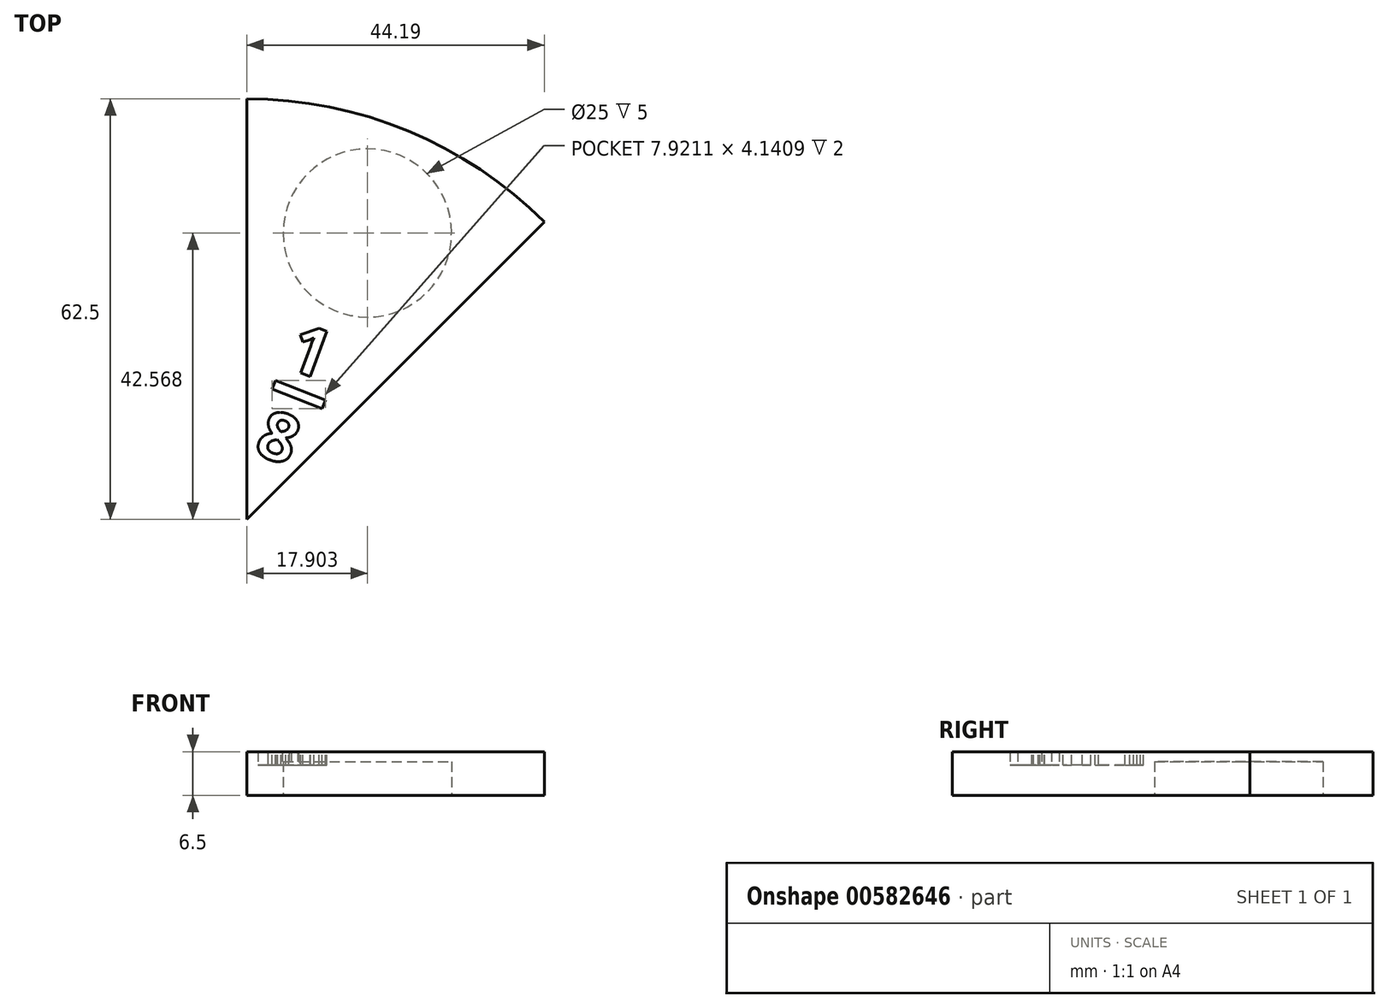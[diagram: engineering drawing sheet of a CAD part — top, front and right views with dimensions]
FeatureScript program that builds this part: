
annotation { "Feature Type Name" : "Feature", "Feature Type Description" : "" }
export const myFeature = defineFeature(function(context is Context, id is Id, definition is map)
    precondition{}
    {
        {
            var Q0;
            Q0=qCreatedBy(makeId("Top.planeOp"),FACE);
            var sketch = newSketch(context, id + "F0", { "sketchPlane" : qUnion([Q0])});
            skArc(sketch, "E0", {"start": v(44.2, 44.2) * mm, "mid": v(23.92, 57.74) * mm, "end": v(0, 62.5) * mm});
            skLineSegment(sketch, "E1", {"start": v(0, 62.5) * mm, "end": v(0, 0) * mm});
            skLineSegment(sketch, "E2", {"start": v(44.2, 44.2) * mm, "end": v(0, 0) * mm});
            skSolve(sketch);
        }
        {
            var Q0;
            Q0=makeQuery(id+"F0.imprint","IMPRINT",FACE,{"disambiguationData":[TD([[makeQuery(id+"F0.imprint","IMPRINT",EDGE,{"derivedFrom":sQuery(id+"F0.wireOp",EDGE,"E0")}),1.0]])]});
            extrude(context, id + "F1", {"entities" : qUnion([Q0]), "depth" : 6.5 * mm, "offsetDistance" : 25 * mm});
        }
        {
            var Q0;
            Q0=makeQuery(id+"F1.opExtrude","CAP_FACE",FACE,{"disambiguationData":[OSD([sQuery(id+"F0.wireOp",EDGE,"E0"),sQuery(id+"F0.wireOp",EDGE,"E1"),sQuery(id+"F0.wireOp",EDGE,"E2")])],"isStart":true});
            var sketch = newSketch(context, id + "F2", { "sketchPlane" : qUnion([Q0])});
            skCircle(sketch, "E3", {"center": v(17.9, -42.57) * mm, "radius": 12.5 * mm});
            skSolve(sketch);
        }
        {
            var Q0;
            Q0=makeQuery(id+"F2.imprint","IMPRINT",FACE,{"disambiguationData":[TD([[makeQuery(id+"F2.imprint","IMPRINT",EDGE,{"derivedFrom":sQuery(id+"F2.wireOp",EDGE,"E3")}),1.0]])]});
            extrude(context, id + "F3", {"entities" : qUnion([Q0]), "operationType" : NewBodyOperationType.REMOVE, "oppositeDirection" : true, "depth" : 5 * mm, "offsetDistance" : 25 * mm});
        }
        {
            var Q0;
            Q0=makeQuery(id+"F1.opExtrude","CAP_FACE",FACE,{"disambiguationData":[OSD([sQuery(id+"F0.wireOp",EDGE,"E0"),sQuery(id+"F0.wireOp",EDGE,"E1"),sQuery(id+"F0.wireOp",EDGE,"E2")])],"isStart":false});
            var sketch = newSketch(context, id + "F4", { "sketchPlane" : qUnion([Q0])});
            skText(sketch, "E4", { "text": "1\n8", "fontName": "OpenSans-Bold.ttf"});
            const initialGuessF4  = {"E4": [0.00555, 0.02268, 0.93855, -0.34515, 0.00721]};
            skSetInitialGuess(sketch, initialGuessF4);
            skSolve(sketch);
        }
        {
            var Q0;
            Q0 = qSketchRegion(id + "F4", true);
            extrude(context, id + "F5", {"entities" : qUnion([Q0]), "operationType" : NewBodyOperationType.REMOVE, "oppositeDirection" : true, "depth" : 2 * mm, "offsetDistance" : 25 * mm});
        }
        {
            var Q0;
            {var subQ0=sQuery(id+"F0.wireOp",EDGE,"E2");var subQ1=sQuery(id+"F0.wireOp",EDGE,"E1");var subQ2=sQuery(id+"F0.wireOp",EDGE,"E0");Q0=makeQuery(id+"F5.boolean.opBoolean","SPLIT",FACE,{"disambiguationData":[TD([makeQuery(id+"F1.opExtrude","SWEPT_FACE",FACE,{"disambiguationData":[OSD([subQ2])]})])],"derivedFrom":makeQuery(id+"F1.opExtrude","CAP_FACE",FACE,{"disambiguationData":[OSD([subQ2,subQ1,subQ0])],"isStart":false})});}
            var sketch = newSketch(context, id + "F6", { "sketchPlane" : qUnion([Q0])});
            skLineSegment(sketch, "E5", {"start": v(3.75, 19.36) * mm, "end": v(11.18, 16.49) * mm});
            skLineSegment(sketch, "E6", {"start": v(11.18, 16.49) * mm, "end": v(11.67, 17.76) * mm});
            skLineSegment(sketch, "E7", {"start": v(3.75, 19.36) * mm, "end": v(4.24, 20.63) * mm});
            skLineSegment(sketch, "E8", {"start": v(4.24, 20.63) * mm, "end": v(11.67, 17.76) * mm});
            skSolve(sketch);
        }
        {
            var Q0;
            Q0 = qSketchRegion(id + "F6", true);
            extrude(context, id + "F7", {"entities" : qUnion([Q0]), "operationType" : NewBodyOperationType.REMOVE, "oppositeDirection" : true, "depth" : 2 * mm, "offsetDistance" : 25 * mm});
        }
    });
